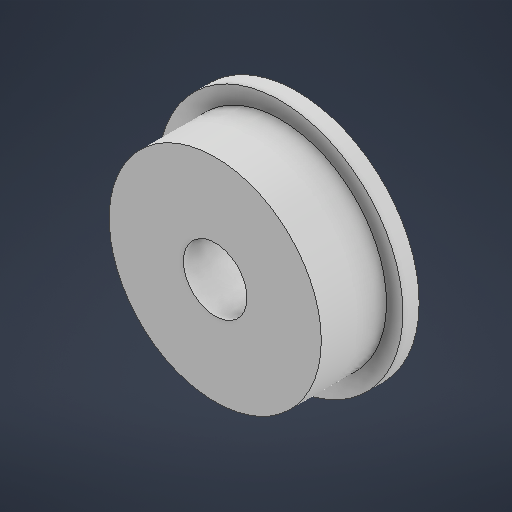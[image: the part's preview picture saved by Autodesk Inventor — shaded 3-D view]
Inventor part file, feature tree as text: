
AUTODESK INVENTOR PART (.ipt)
format: ipt  version: 2025.1 (Build 291241000, 241)  size: 216,064 bytes
history: native  units: mm
features: extrude x2, sketch x1
ambient origin geometry x8: Origin, YZ Plane, XZ Plane, XY Plane, X Axis, Y Axis, Z Axis, Center Point
bodies: Solid1 (feature_tree)
feature tree (3):
  sketch  "Sketch1"  dims[d0=3.9mm d1=13.0mm d2=15.0mm d3=1.0mm d4=0.0mm d5=5.0mm d6=0.0mm d7=0.9mm]
  extrude  "Extrusion1"  Depth=5.0mm
  extrude  "Extrusion2"  Depth=5.0mm
